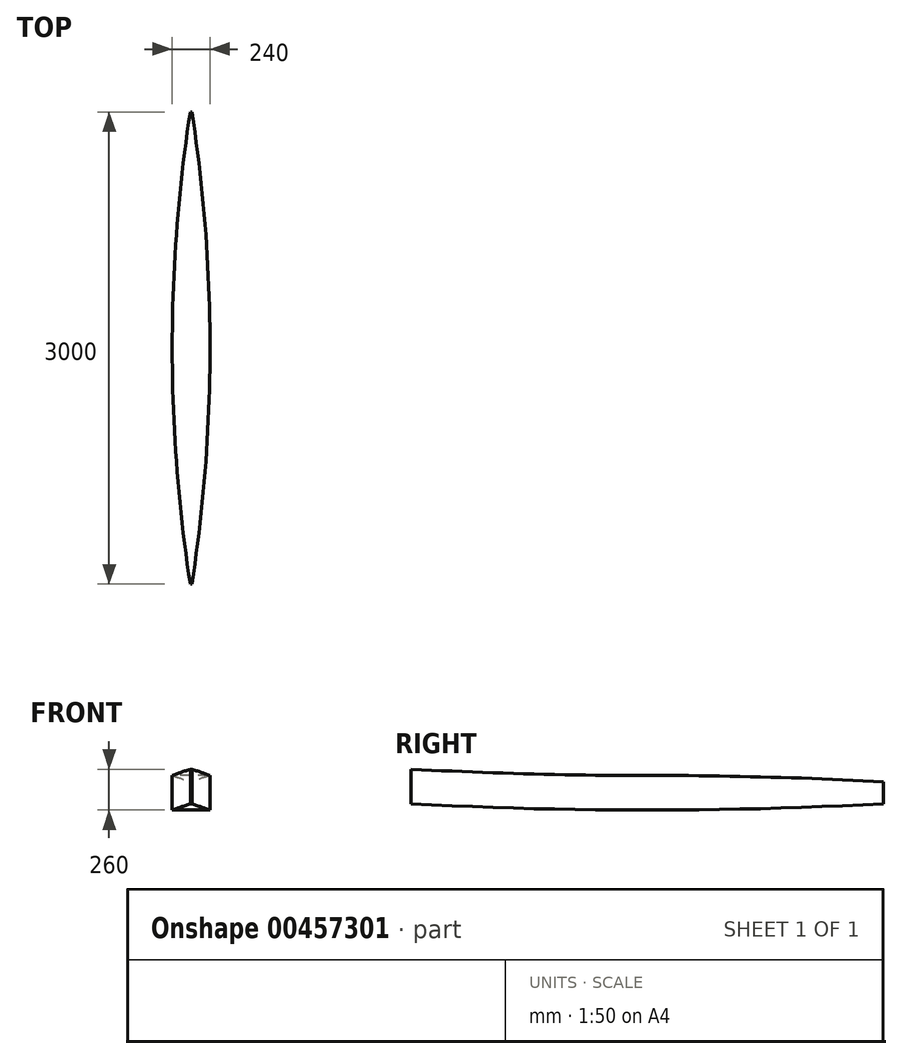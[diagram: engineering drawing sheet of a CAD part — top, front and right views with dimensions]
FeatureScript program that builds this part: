
annotation { "Feature Type Name" : "Feature", "Feature Type Description" : "" }
export const myFeature = defineFeature(function(context is Context, id is Id, definition is map)
    precondition{}
    {
        {
            var Q0;
            Q0=qCreatedBy(makeId("Top.planeOp"),FACE);
            var sketch = newSketch(context, id + "F0", { "sketchPlane" : qUnion([Q0])});
            skLineSegment(sketch, "E0", {"start": v(0, 0) * mm, "end": v(0, 1500) * mm});
            skLineSegment(sketch, "E1", {"start": v(0, 0) * mm, "end": v(120, 0) * mm});
            skLineSegment(sketch, "E2", {"start": v(120, 0) * mm, "end": v(120, -200) * mm, "construction": true});
            skLineSegment(sketch, "E3", {"start": v(0, 1500) * mm, "end": v(5, 1500) * mm});
            skArc(sketch, "E4", {"start": v(120, 0) * mm, "mid": v(91.2, 752.2) * mm, "end": v(5, 1500) * mm});
            skSolve(sketch);
        }
        {
            var Q0;
            Q0 = qSketchRegion(id + "F0", true);
            extrude(context, id + "F1", {"entities" : qUnion([Q0]), "depth" : 110 * mm});
        }
        {
            var Q0;
            Q0=qCreatedBy(makeId("Right.planeOp"),FACE);
            var sketch = newSketch(context, id + "F2", { "sketchPlane" : qUnion([Q0])});
            skLineSegment(sketch, "E5.0", {"start": v(0, 0) * mm, "end": v(1500, 0) * mm});
            skLineSegment(sketch, "E6", {"start": v(1500, 0) * mm, "end": v(1500, 40) * mm});
            skLineSegment(sketch, "E7", {"start": v(0, 0) * mm, "end": v(-216.61, 0) * mm, "construction": true});
            skArc(sketch, "E8", {"start": v(0, 0) * mm, "mid": v(750.27, 10) * mm, "end": v(1500, 40) * mm});
            skSolve(sketch);
        }
        {
            var Q0;
            Q0 = qSketchRegion(id + "F2", true);
            extrude(context, id + "F3", {"entities" : qUnion([Q0]), "operationType" : NewBodyOperationType.REMOVE, "depth" : 200 * mm});
        }
        {
            var Q0;
            Q0=makeQuery(id+"F1.opExtrude","SWEPT_BODY",BODY,{"disambiguationData":[OSD([sQuery(id+"F0.wireOp",EDGE,"E0"),sQuery(id+"F0.wireOp",EDGE,"E1"),sQuery(id+"F0.wireOp",EDGE,"E3"),sQuery(id+"F0.wireOp",EDGE,"E4")])]});
            var Q1;
            Q1=makeQuery(id+"F1.opExtrude","CAP_FACE",FACE,{"disambiguationData":[OSD([sQuery(id+"F0.wireOp",EDGE,"E0"),sQuery(id+"F0.wireOp",EDGE,"E1"),sQuery(id+"F0.wireOp",EDGE,"E3"),sQuery(id+"F0.wireOp",EDGE,"E4")])],"isStart":false});
            mirror(context, id + "F4", {"operationType" : NewBodyOperationType.ADD, "entities" : qUnion([Q0]), "mirrorPlane" : qUnion([Q1])});
        }
        {
            var Q0;
            Q0=makeQuery(id+"F1.opExtrude","SWEPT_BODY",BODY,{"disambiguationData":[OSD([sQuery(id+"F0.wireOp",EDGE,"E0"),sQuery(id+"F0.wireOp",EDGE,"E1"),sQuery(id+"F0.wireOp",EDGE,"E3"),sQuery(id+"F0.wireOp",EDGE,"E4")])]});
            var Q1;
            Q1=qCreatedBy(makeId("Right.planeOp"),FACE);
            mirror(context, id + "F5", {"operationType" : NewBodyOperationType.ADD, "entities" : qUnion([Q0]), "mirrorPlane" : qUnion([Q1])});
        }
        {
            var Q0;
            Q0=makeQuery(id+"F1.opExtrude","SWEPT_BODY",BODY,{"disambiguationData":[OSD([sQuery(id+"F0.wireOp",EDGE,"E0"),sQuery(id+"F0.wireOp",EDGE,"E1"),sQuery(id+"F0.wireOp",EDGE,"E3"),sQuery(id+"F0.wireOp",EDGE,"E4")])]});
            var Q1;
            Q1=qCreatedBy(makeId("Front.planeOp"),FACE);
            mirror(context, id + "F6", {"operationType" : NewBodyOperationType.ADD, "entities" : qUnion([Q0]), "mirrorPlane" : qUnion([Q1])});
        }
        {
            var Q0;
            Q0=qCreatedBy(makeId("Right.planeOp"),FACE);
            var sketch = newSketch(context, id + "F7", { "sketchPlane" : qUnion([Q0])});
            skLineSegment(sketch, "E9", {"start": v(2.14, 220) * mm, "end": v(7.8, 802.16) * mm, "construction": true});
            skArc(sketch, "E10.0", {"start": v(-1500, 180) * mm, "mid": v(-749.2, 210.03) * mm, "end": v(2.14, 220) * mm});
            skPoint(sketch, "E11.orphan", {"position": v(1500, 180) * mm});
            skLineSegment(sketch, "E12", {"start": v(-1500, 180) * mm, "end": v(-1500, 260) * mm});
            skLineSegment(sketch, "E13", {"start": v(2.14, 220) * mm, "end": v(773.8, 220) * mm, "construction": true});
            skArc(sketch, "E14", {"start": v(2.14, 220) * mm, "mid": v(-749.2, 230) * mm, "end": v(-1500, 260) * mm});
            skSolve(sketch);
        }
        {
            var Q0;
            Q0 = qSketchRegion(id + "F7", true);
            extrude(context, id + "F8", {"entities" : qUnion([Q0]), "operationType" : NewBodyOperationType.ADD, "depth" : 200 * mm, "hasSecondDirection" : true, "secondDirectionOppositeDirection" : true, "secondDirectionDepth" : 200 * mm});
        }
        {
            var Q0;
            Q0=qCreatedBy(makeId("Top.planeOp"),FACE);
            var sketch = newSketch(context, id + "F9", { "sketchPlane" : qUnion([Q0])});
            skLineSegment(sketch, "E15.0", {"start": v(200, -1500) * mm, "end": v(5, -1500) * mm});
            skLineSegment(sketch, "E16.0", {"start": v(-5, -1500) * mm, "end": v(-200, -1500) * mm});
            skLineSegment(sketch, "E17.0", {"start": v(200, -1500) * mm, "end": v(200, 0) * mm});
            skArc(sketch, "E18.0.1", {"start": v(5, -1500) * mm, "mid": v(91.2, -752.2) * mm, "end": v(120, 0) * mm});
            skLineSegment(sketch, "E18.0.2", {"start": v(120, 0) * mm, "end": v(200, 0) * mm});
            skLineSegment(sketch, "E18.0.3", {"start": v(200, 0) * mm, "end": v(200, -1500) * mm});
            skLineSegment(sketch, "E19.0", {"start": v(-200, -1500) * mm, "end": v(-200, 0) * mm});
            skPoint(sketch, "E20.0", {"position": v(-120, 0) * mm});
            skLineSegment(sketch, "E21.0", {"start": v(-120, 0) * mm, "end": v(-200, 0) * mm});
            skArc(sketch, "E22.0", {"start": v(-5, -1500) * mm, "mid": v(-120, 0) * mm, "end": v(-5, 1500) * mm});
            skSolve(sketch);
        }
        {
            var Q0;
            Q0 = qSketchRegion(id + "F9", true);
            extrude(context, id + "F10", {"entities" : qUnion([Q0]), "operationType" : NewBodyOperationType.REMOVE, "depth" : 300 * mm});
        }
    });
